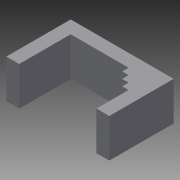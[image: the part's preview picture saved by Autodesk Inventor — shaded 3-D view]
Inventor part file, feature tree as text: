
AUTODESK INVENTOR PART (.ipt)
format: ipt  version: 2013 SP2 (Build 170200200, 200)  size: 88,064 bytes
history: native  units: in
note: dims shown in document units (in); Inventor stores cm internally (conversion verified against a paired STEP export)
features: extrude x1, sketch x1
ambient origin geometry x8: Origin, YZ Plane, XZ Plane, XY Plane, X Axis, Y Axis, Z Axis, Center Point
bodies: Solid1 (feature_tree)
feature tree (2):
  extrude  "Extrusion1"  Depth=1.25in
  sketch  "Sketch1"  dims[d0=2.0in d1=1.25in d2=0.25in d3=0.25in d4=1.5in d5=1.0in d6=0.25in d7=0.25in d8=0.125in d9=0.125in d10=0.125in d11=0.125in d12=0.75in d13=0.0in]
